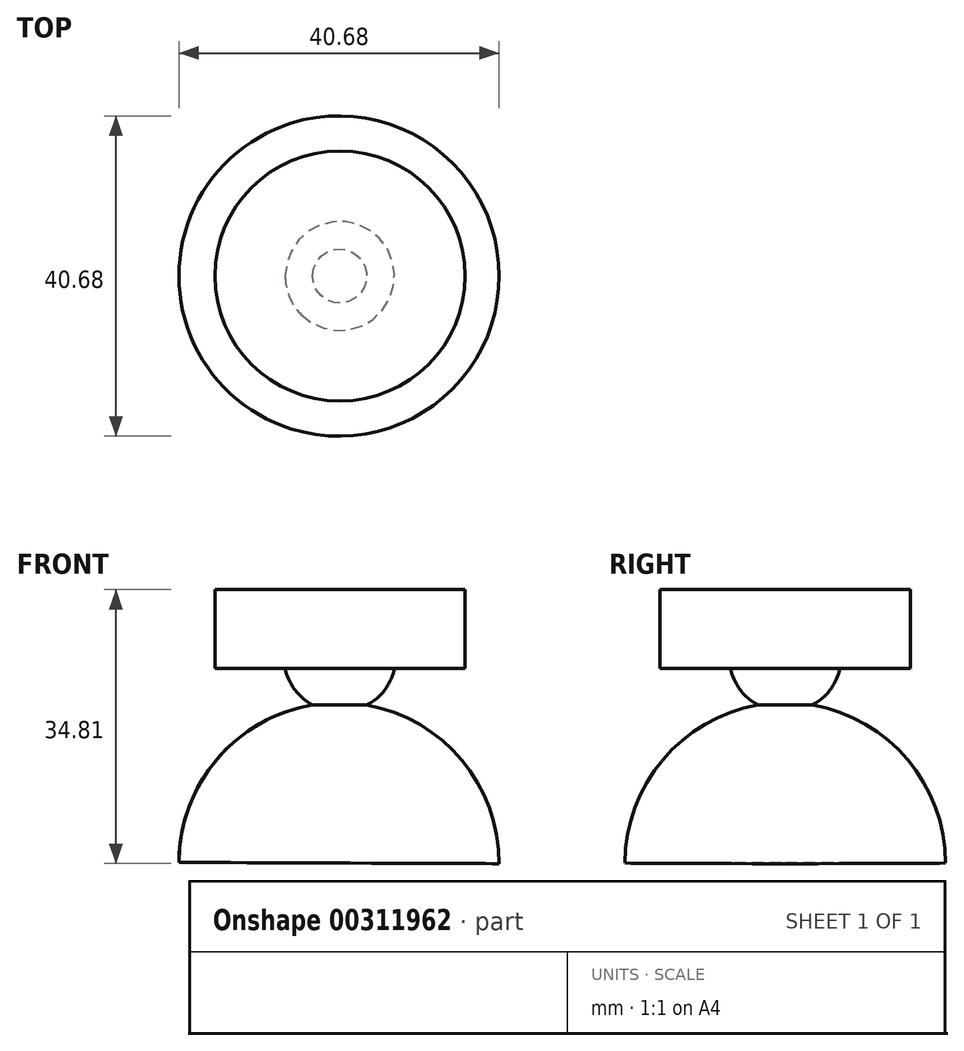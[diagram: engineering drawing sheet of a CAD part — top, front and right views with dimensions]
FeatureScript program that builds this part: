
annotation { "Feature Type Name" : "Feature", "Feature Type Description" : "" }
export const myFeature = defineFeature(function(context is Context, id is Id, definition is map)
    precondition{}
    {
        {
            var Q0;
            Q0=qCreatedBy(makeId("Front.planeOp"),FACE);
            var sketch = newSketch(context, id + "F0", { "sketchPlane" : qUnion([Q0])});
            skArc(sketch, "E0", {"start": v(-3.49, -4.65) * mm, "mid": v(-15.63, -11.55) * mm, "end": v(-20.47, -24.65) * mm});
            skArc(sketch, "E1", {"start": v(0, 8.14) * mm, "mid": v(-6.86, 3.14) * mm, "end": v(-3.49, -4.65) * mm});
            skLineSegment(sketch, "E2", {"start": v(-0.13, -24.71) * mm, "end": v(0, 8.14) * mm});
            skLineSegment(sketch, "E3", {"start": v(-20.47, -24.65) * mm, "end": v(-0.13, -24.71) * mm});
            skSolve(sketch);
        }
        {
            var Q0;
            Q0 = qSketchRegion(id + "F0", true);
            var Q1;
            Q1=sQuery(id+"F0.wireOp",EDGE,"E2");
            revolve(context, id + "F1", {"entities" : qUnion([Q0]), "axis" : qUnion([Q1]), "revolveType" : RevolveType.FULL});
        }
        {
            var Q0;
            Q0=qCreatedBy(makeId("Top.planeOp"),FACE);
            var sketch = newSketch(context, id + "F2", { "sketchPlane" : qUnion([Q0])});
            skCircle(sketch, "E4", {"center": v(0, 0) * mm, "radius": 15.9 * mm});
            skSolve(sketch);
        }
        {
            var Q0;
            Q0 = qSketchRegion(id + "F2", true);
            extrude(context, id + "F3", {"entities" : qUnion([Q0]), "operationType" : NewBodyOperationType.ADD, "depth" : 10 * mm});
        }
    });
